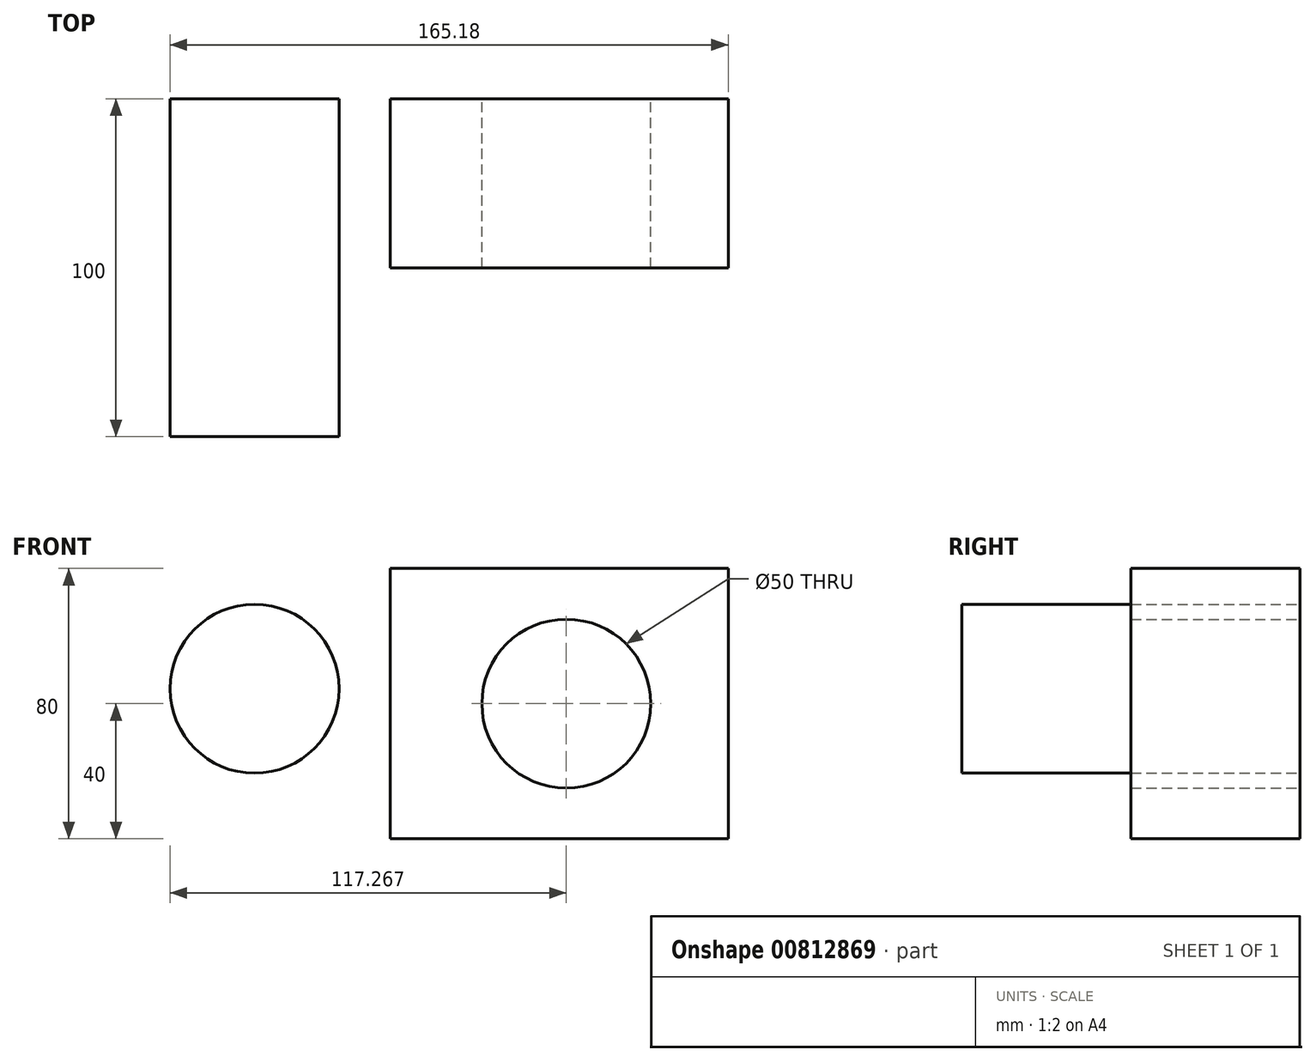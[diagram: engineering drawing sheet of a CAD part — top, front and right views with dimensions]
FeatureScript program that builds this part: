
annotation { "Feature Type Name" : "Feature", "Feature Type Description" : "" }
export const myFeature = defineFeature(function(context is Context, id is Id, definition is map)
    precondition{}
    {
        {
            var Q0;
            Q0=qCreatedBy(makeId("Front.planeOp"),FACE);
            var sketch = newSketch(context, id + "F0", { "sketchPlane" : qUnion([Q0])});
            skLineSegment(sketch, "E0.bottom", {"start": v(-50, 40) * mm, "end": v(50, 40) * mm});
            skLineSegment(sketch, "E0.top", {"start": v(-50, -40) * mm, "end": v(50, -40) * mm});
            skLineSegment(sketch, "E0.left", {"start": v(-50, 40) * mm, "end": v(-50, -40) * mm});
            skLineSegment(sketch, "E0.right", {"start": v(50, 40) * mm, "end": v(50, -40) * mm});
            skSolve(sketch);
        }
        {
            var Q0;
            Q0=makeQuery(id+"F0.imprint","IMPRINT",FACE,{"disambiguationData":[TD([[makeQuery(id+"F0.imprint","IMPRINT",EDGE,{"derivedFrom":sQuery(id+"F0.wireOp",EDGE,"E0.bottom")}),-1.0]])]});
            extrude(context, id + "F1", {"entities" : qUnion([Q0]), "depth" : 50 * mm, "offsetDistance" : 25 * mm});
        }
        {
            var Q0;
            Q0=qCreatedBy(makeId("Front.planeOp"),FACE);
            var sketch = newSketch(context, id + "F2", { "sketchPlane" : qUnion([Q0])});
            skCircle(sketch, "E1", {"center": v(2.09, 0) * mm, "radius": 25 * mm});
            skSolve(sketch);
        }
        {
            var Q0;
            Q0=makeQuery(id+"F2.imprint","IMPRINT",FACE,{"disambiguationData":[TD([[makeQuery(id+"F2.imprint","IMPRINT",EDGE,{"derivedFrom":sQuery(id+"F2.wireOp",EDGE,"E1")}),1.0]])]});
            extrude(context, id + "F3", {"entities" : qUnion([Q0]), "operationType" : NewBodyOperationType.REMOVE, "depth" : 50 * mm, "offsetDistance" : 25 * mm});
        }
        {
            var Q0;
            Q0=qCreatedBy(makeId("Front.planeOp"),FACE);
            var sketch = newSketch(context, id + "F4", { "sketchPlane" : qUnion([Q0])});
            skCircle(sketch, "E2", {"center": v(-90.18, 4.42) * mm, "radius": 25 * mm});
            skSolve(sketch);
        }
        {
            var Q0;
            Q0 = qSketchRegion(id + "F4", true);
            extrude(context, id + "F5", {"entities" : qUnion([Q0]), "depth" : 100 * mm, "offsetDistance" : 25 * mm});
        }
    });
